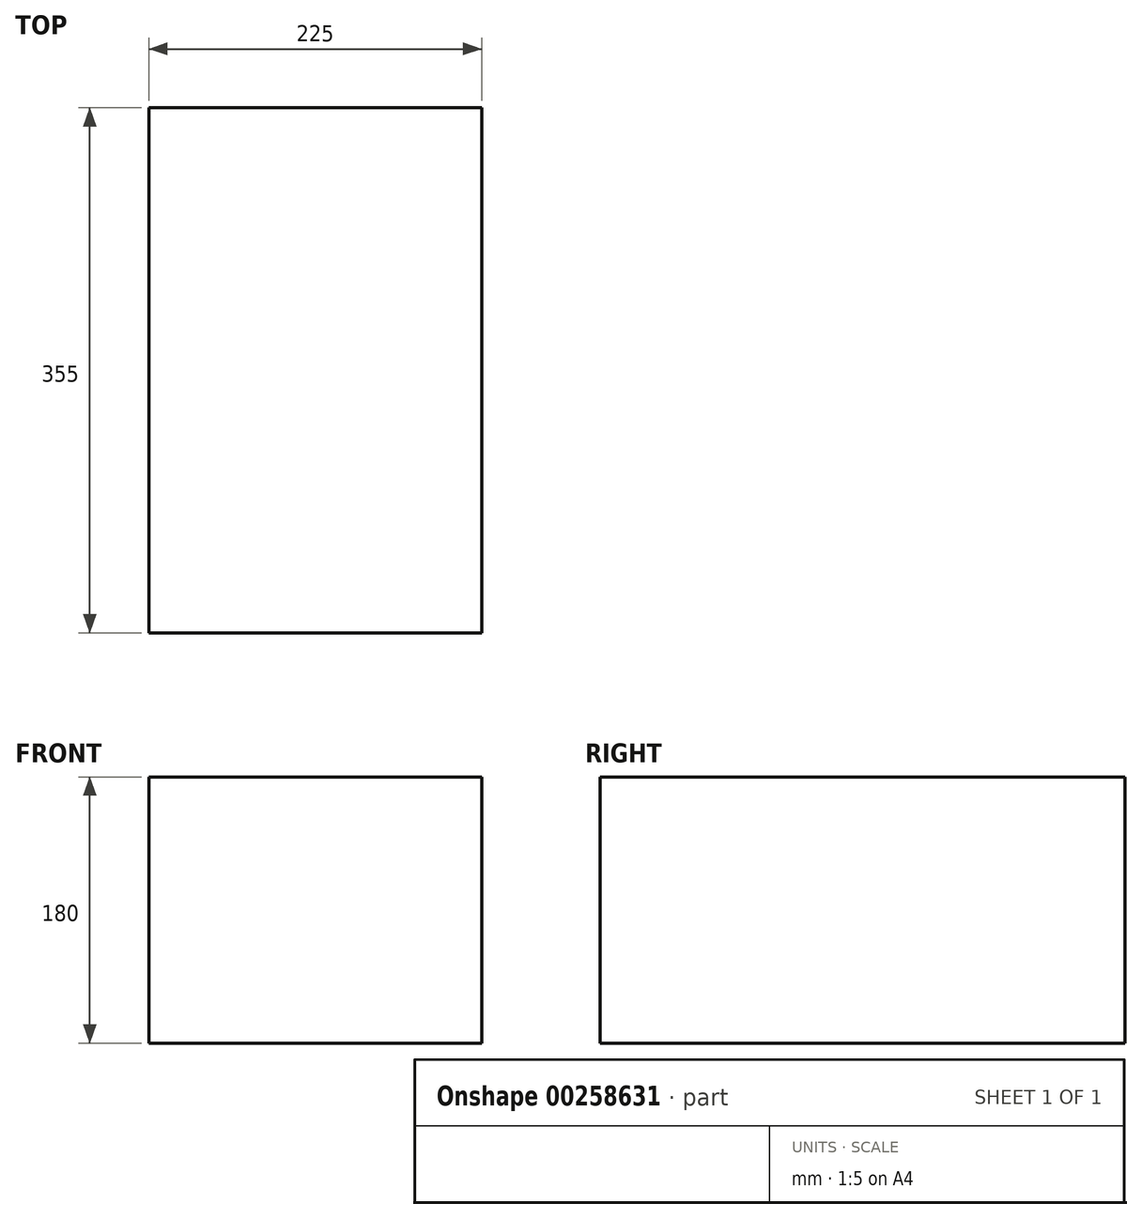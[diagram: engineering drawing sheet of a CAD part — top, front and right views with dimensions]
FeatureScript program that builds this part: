
annotation { "Feature Type Name" : "Feature", "Feature Type Description" : "" }
export const myFeature = defineFeature(function(context is Context, id is Id, definition is map)
    precondition{}
    {
        {
            var Q0;
            Q0=qCreatedBy(makeId("Top.planeOp"),FACE);
            var sketch = newSketch(context, id + "F0", { "sketchPlane" : qUnion([Q0])});
            skLineSegment(sketch, "E0.bottom", {"start": v(0, 0) * mm, "end": v(225, 0) * mm});
            skLineSegment(sketch, "E0.top", {"start": v(0, 355) * mm, "end": v(225, 355) * mm});
            skLineSegment(sketch, "E0.left", {"start": v(0, 0) * mm, "end": v(0, 355) * mm});
            skLineSegment(sketch, "E0.right", {"start": v(225, 0) * mm, "end": v(225, 355) * mm});
            skSolve(sketch);
        }
        {
            var Q0;
            Q0 = qSketchRegion(id + "F0", true);
            extrude(context, id + "F1", {"entities" : qUnion([Q0]), "depth" : 180 * mm});
        }
    });
